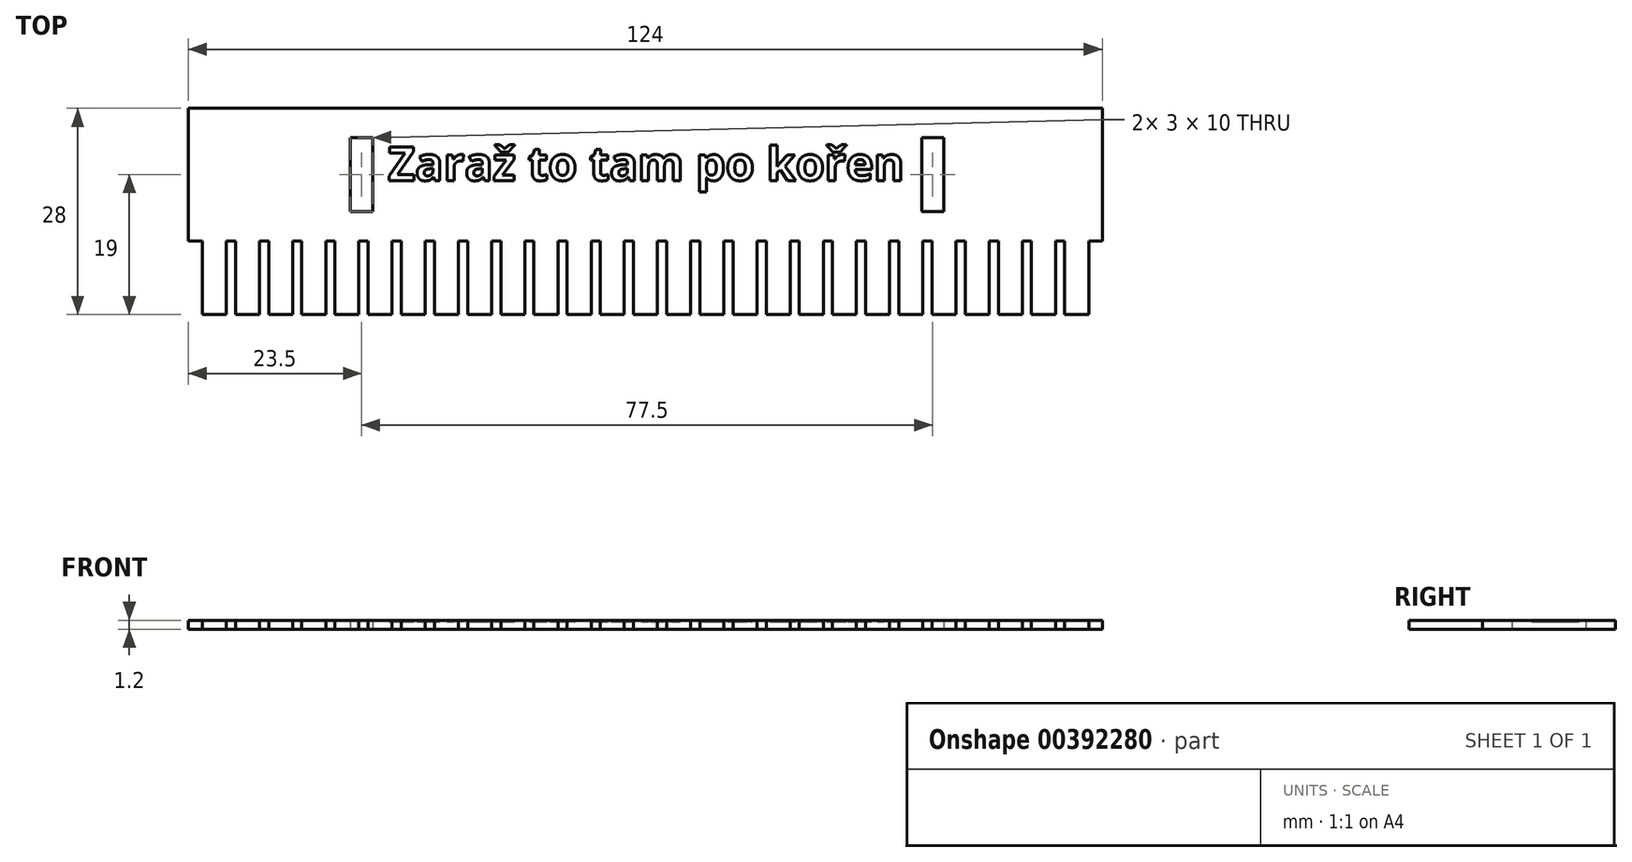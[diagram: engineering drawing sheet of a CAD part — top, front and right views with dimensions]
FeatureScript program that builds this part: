
annotation { "Feature Type Name" : "Feature", "Feature Type Description" : "" }
export const myFeature = defineFeature(function(context is Context, id is Id, definition is map)
    precondition{}
    {
        {
            var Q0;
            Q0=qCreatedBy(makeId("Top.planeOp"),FACE);
            var sketch = newSketch(context, id + "F0", { "sketchPlane" : qUnion([Q0])});
            skLineSegment(sketch, "E0.bottom", {"start": v(62, -14) * mm, "end": v(-62, -14) * mm});
            skLineSegment(sketch, "E0.top", {"start": v(62, 14) * mm, "end": v(-62, 14) * mm});
            skLineSegment(sketch, "E0.left", {"start": v(62, -14) * mm, "end": v(62, 14) * mm});
            skLineSegment(sketch, "E0.right", {"start": v(-62, -14) * mm, "end": v(-62, 14) * mm});
            skPoint(sketch, "E0.middle", {"position": v(0, 0) * mm});
            skLineSegment(sketch, "E1.bottom", {"start": v(-62, -14) * mm, "end": v(-60.1, -14) * mm});
            skLineSegment(sketch, "E1.top", {"start": v(-62, -4) * mm, "end": v(-60.1, -4) * mm});
            skLineSegment(sketch, "E1.left", {"start": v(-62, -14) * mm, "end": v(-62, -4) * mm});
            skLineSegment(sketch, "E1.right", {"start": v(-60.1, -14) * mm, "end": v(-60.1, -4) * mm});
            skLineSegment(sketch, "E2.bottom", {"start": v(-60.1, -14) * mm, "end": v(-56.85, -14) * mm});
            skLineSegment(sketch, "E2.right", {"start": v(-56.85, -14) * mm, "end": v(-56.85, -4) * mm});
            skLineSegment(sketch, "E3.bottom", {"start": v(-56.85, -14) * mm, "end": v(-55.6, -14) * mm});
            skLineSegment(sketch, "E3.top", {"start": v(-56.85, -4) * mm, "end": v(-55.6, -4) * mm});
            skLineSegment(sketch, "E3.right", {"start": v(-55.6, -14) * mm, "end": v(-55.6, -4) * mm});
            skLineSegment(sketch, "E4.bottom", {"start": v(-55.6, -14) * mm, "end": v(-52.35, -14) * mm});
            skLineSegment(sketch, "E4.right", {"start": v(-52.35, -14) * mm, "end": v(-52.35, -4) * mm});
            skLineSegment(sketch, "E5.bottom", {"start": v(-52.35, -14) * mm, "end": v(-51.1, -14) * mm});
            skLineSegment(sketch, "E5.top", {"start": v(-52.35, -4) * mm, "end": v(-51.1, -4) * mm});
            skLineSegment(sketch, "E5.right", {"start": v(-51.1, -14) * mm, "end": v(-51.1, -4) * mm});
            skLineSegment(sketch, "E6.bottom", {"start": v(-51.1, -14) * mm, "end": v(-47.85, -14) * mm});
            skLineSegment(sketch, "E6.right", {"start": v(-47.85, -14) * mm, "end": v(-47.85, -4) * mm});
            skLineSegment(sketch, "E7.bottom", {"start": v(-47.85, -14) * mm, "end": v(-46.6, -14) * mm});
            skLineSegment(sketch, "E7.top", {"start": v(-47.85, -4) * mm, "end": v(-46.6, -4) * mm});
            skLineSegment(sketch, "E7.right", {"start": v(-46.6, -14) * mm, "end": v(-46.6, -4) * mm});
            skLineSegment(sketch, "E8.bottom", {"start": v(-46.6, -14) * mm, "end": v(-43.35, -14) * mm});
            skLineSegment(sketch, "E8.right", {"start": v(-43.35, -14) * mm, "end": v(-43.35, -4) * mm});
            skLineSegment(sketch, "E9.bottom", {"start": v(-43.35, -14) * mm, "end": v(-42.1, -14) * mm});
            skLineSegment(sketch, "E9.top", {"start": v(-43.35, -4) * mm, "end": v(-42.1, -4) * mm});
            skLineSegment(sketch, "E9.right", {"start": v(-42.1, -14) * mm, "end": v(-42.1, -4) * mm});
            skLineSegment(sketch, "E10.bottom", {"start": v(-42.1, -14) * mm, "end": v(-38.85, -14) * mm});
            skLineSegment(sketch, "E10.right", {"start": v(-38.85, -14) * mm, "end": v(-38.85, -4) * mm});
            skLineSegment(sketch, "E11.bottom", {"start": v(-38.85, -14) * mm, "end": v(-37.6, -14) * mm});
            skLineSegment(sketch, "E11.top", {"start": v(-38.85, -4) * mm, "end": v(-37.6, -4) * mm});
            skLineSegment(sketch, "E11.right", {"start": v(-37.6, -14) * mm, "end": v(-37.6, -4) * mm});
            skLineSegment(sketch, "E12.bottom", {"start": v(-37.6, -14) * mm, "end": v(-34.35, -14) * mm});
            skLineSegment(sketch, "E12.right", {"start": v(-34.35, -14) * mm, "end": v(-34.35, -4) * mm});
            skLineSegment(sketch, "E13.bottom", {"start": v(-34.35, -14) * mm, "end": v(-33.1, -14) * mm});
            skLineSegment(sketch, "E13.top", {"start": v(-34.35, -4) * mm, "end": v(-33.1, -4) * mm});
            skLineSegment(sketch, "E13.right", {"start": v(-33.1, -14) * mm, "end": v(-33.1, -4) * mm});
            skLineSegment(sketch, "E14.bottom", {"start": v(-33.1, -14) * mm, "end": v(-29.85, -14) * mm});
            skLineSegment(sketch, "E14.right", {"start": v(-29.85, -14) * mm, "end": v(-29.85, -4) * mm});
            skLineSegment(sketch, "E15.bottom", {"start": v(-29.85, -14) * mm, "end": v(-28.6, -14) * mm});
            skLineSegment(sketch, "E15.top", {"start": v(-29.85, -4) * mm, "end": v(-28.6, -4) * mm});
            skLineSegment(sketch, "E15.right", {"start": v(-28.6, -14) * mm, "end": v(-28.6, -4) * mm});
            skLineSegment(sketch, "E16.bottom", {"start": v(-28.6, -14) * mm, "end": v(-25.35, -14) * mm});
            skLineSegment(sketch, "E16.right", {"start": v(-25.35, -14) * mm, "end": v(-25.35, -4) * mm});
            skLineSegment(sketch, "E17.bottom", {"start": v(-25.35, -14) * mm, "end": v(-24.1, -14) * mm});
            skLineSegment(sketch, "E17.top", {"start": v(-25.35, -4) * mm, "end": v(-24.1, -4) * mm});
            skLineSegment(sketch, "E17.right", {"start": v(-24.1, -14) * mm, "end": v(-24.1, -4) * mm});
            skLineSegment(sketch, "E18.bottom", {"start": v(-24.1, -14) * mm, "end": v(-20.85, -14) * mm});
            skLineSegment(sketch, "E18.right", {"start": v(-20.85, -14) * mm, "end": v(-20.85, -4) * mm});
            skLineSegment(sketch, "E19.bottom", {"start": v(-20.85, -14) * mm, "end": v(-19.6, -14) * mm});
            skLineSegment(sketch, "E19.top", {"start": v(-20.85, -4) * mm, "end": v(-19.6, -4) * mm});
            skLineSegment(sketch, "E19.right", {"start": v(-19.6, -14) * mm, "end": v(-19.6, -4) * mm});
            skLineSegment(sketch, "E20.bottom", {"start": v(-19.6, -14) * mm, "end": v(-16.35, -14) * mm});
            skLineSegment(sketch, "E20.right", {"start": v(-16.35, -14) * mm, "end": v(-16.35, -4) * mm});
            skLineSegment(sketch, "E21.bottom", {"start": v(-16.35, -14) * mm, "end": v(-15.1, -14) * mm});
            skLineSegment(sketch, "E21.top", {"start": v(-16.35, -4) * mm, "end": v(-15.1, -4) * mm});
            skLineSegment(sketch, "E21.right", {"start": v(-15.1, -14) * mm, "end": v(-15.1, -4) * mm});
            skLineSegment(sketch, "E22.bottom", {"start": v(-15.1, -14) * mm, "end": v(-11.85, -14) * mm});
            skLineSegment(sketch, "E22.right", {"start": v(-11.85, -14) * mm, "end": v(-11.85, -4) * mm});
            skLineSegment(sketch, "E23.bottom", {"start": v(-11.85, -14) * mm, "end": v(-10.6, -14) * mm});
            skLineSegment(sketch, "E23.top", {"start": v(-11.85, -4) * mm, "end": v(-10.6, -4) * mm});
            skLineSegment(sketch, "E23.right", {"start": v(-10.6, -14) * mm, "end": v(-10.6, -4) * mm});
            skLineSegment(sketch, "E24.bottom", {"start": v(-10.6, -14) * mm, "end": v(-7.35, -14) * mm});
            skLineSegment(sketch, "E24.right", {"start": v(-7.35, -14) * mm, "end": v(-7.35, -4) * mm});
            skLineSegment(sketch, "E25.bottom", {"start": v(-7.35, -14) * mm, "end": v(-6.1, -14) * mm});
            skLineSegment(sketch, "E25.top", {"start": v(-7.35, -4) * mm, "end": v(-6.1, -4) * mm});
            skLineSegment(sketch, "E25.right", {"start": v(-6.1, -14) * mm, "end": v(-6.1, -4) * mm});
            skLineSegment(sketch, "E26.bottom", {"start": v(-6.1, -14) * mm, "end": v(-2.85, -14) * mm});
            skLineSegment(sketch, "E26.right", {"start": v(-2.85, -14) * mm, "end": v(-2.85, -4) * mm});
            skLineSegment(sketch, "E27.bottom", {"start": v(-2.85, -14) * mm, "end": v(-1.6, -14) * mm});
            skLineSegment(sketch, "E27.top", {"start": v(-2.85, -4) * mm, "end": v(-1.6, -4) * mm});
            skLineSegment(sketch, "E27.right", {"start": v(-1.6, -14) * mm, "end": v(-1.6, -4) * mm});
            skLineSegment(sketch, "E28.bottom", {"start": v(-1.6, -14) * mm, "end": v(1.65, -14) * mm});
            skLineSegment(sketch, "E28.right", {"start": v(1.65, -14) * mm, "end": v(1.65, -4) * mm});
            skLineSegment(sketch, "E29.bottom", {"start": v(1.65, -14) * mm, "end": v(2.9, -14) * mm});
            skLineSegment(sketch, "E29.top", {"start": v(1.65, -4) * mm, "end": v(2.9, -4) * mm});
            skLineSegment(sketch, "E29.right", {"start": v(2.9, -14) * mm, "end": v(2.9, -4) * mm});
            skLineSegment(sketch, "E30.bottom", {"start": v(2.9, -14) * mm, "end": v(6.15, -14) * mm});
            skLineSegment(sketch, "E30.right", {"start": v(6.15, -14) * mm, "end": v(6.15, -4) * mm});
            skLineSegment(sketch, "E31.bottom", {"start": v(6.15, -14) * mm, "end": v(7.4, -14) * mm});
            skLineSegment(sketch, "E31.top", {"start": v(6.15, -4) * mm, "end": v(7.4, -4) * mm});
            skLineSegment(sketch, "E31.right", {"start": v(7.4, -14) * mm, "end": v(7.4, -4) * mm});
            skLineSegment(sketch, "E32.bottom", {"start": v(7.4, -14) * mm, "end": v(10.65, -14) * mm});
            skLineSegment(sketch, "E32.right", {"start": v(10.65, -14) * mm, "end": v(10.65, -4) * mm});
            skLineSegment(sketch, "E33.bottom", {"start": v(10.65, -14) * mm, "end": v(11.9, -14) * mm});
            skLineSegment(sketch, "E33.top", {"start": v(10.65, -4) * mm, "end": v(11.9, -4) * mm});
            skLineSegment(sketch, "E33.right", {"start": v(11.9, -14) * mm, "end": v(11.9, -4) * mm});
            skLineSegment(sketch, "E34.bottom", {"start": v(11.9, -14) * mm, "end": v(15.15, -14) * mm});
            skLineSegment(sketch, "E34.right", {"start": v(15.15, -14) * mm, "end": v(15.15, -4) * mm});
            skLineSegment(sketch, "E35.bottom", {"start": v(15.15, -14) * mm, "end": v(16.4, -14) * mm});
            skLineSegment(sketch, "E35.top", {"start": v(15.15, -4) * mm, "end": v(16.4, -4) * mm});
            skLineSegment(sketch, "E35.right", {"start": v(16.4, -14) * mm, "end": v(16.4, -4) * mm});
            skLineSegment(sketch, "E36.bottom", {"start": v(16.4, -14) * mm, "end": v(19.65, -14) * mm});
            skLineSegment(sketch, "E36.right", {"start": v(19.65, -14) * mm, "end": v(19.65, -4) * mm});
            skLineSegment(sketch, "E37.bottom", {"start": v(19.65, -14) * mm, "end": v(20.9, -14) * mm});
            skLineSegment(sketch, "E37.top", {"start": v(19.65, -4) * mm, "end": v(20.9, -4) * mm});
            skLineSegment(sketch, "E37.right", {"start": v(20.9, -14) * mm, "end": v(20.9, -4) * mm});
            skLineSegment(sketch, "E38.bottom", {"start": v(20.9, -14) * mm, "end": v(24.15, -14) * mm});
            skLineSegment(sketch, "E38.right", {"start": v(24.15, -14) * mm, "end": v(24.15, -4) * mm});
            skLineSegment(sketch, "E39.bottom", {"start": v(24.15, -14) * mm, "end": v(25.4, -14) * mm});
            skLineSegment(sketch, "E39.top", {"start": v(24.15, -4) * mm, "end": v(25.4, -4) * mm});
            skLineSegment(sketch, "E39.right", {"start": v(25.4, -14) * mm, "end": v(25.4, -4) * mm});
            skLineSegment(sketch, "E40.bottom", {"start": v(25.4, -14) * mm, "end": v(28.65, -14) * mm});
            skLineSegment(sketch, "E40.right", {"start": v(28.65, -14) * mm, "end": v(28.65, -4) * mm});
            skLineSegment(sketch, "E41.bottom", {"start": v(28.65, -14) * mm, "end": v(29.9, -14) * mm});
            skLineSegment(sketch, "E41.top", {"start": v(28.65, -4) * mm, "end": v(29.9, -4) * mm});
            skLineSegment(sketch, "E41.right", {"start": v(29.9, -14) * mm, "end": v(29.9, -4) * mm});
            skLineSegment(sketch, "E42.bottom", {"start": v(29.9, -14) * mm, "end": v(33.15, -14) * mm});
            skLineSegment(sketch, "E42.right", {"start": v(33.15, -14) * mm, "end": v(33.15, -4) * mm});
            skLineSegment(sketch, "E43.bottom", {"start": v(33.15, -14) * mm, "end": v(34.4, -14) * mm});
            skLineSegment(sketch, "E43.top", {"start": v(33.15, -4) * mm, "end": v(34.4, -4) * mm});
            skLineSegment(sketch, "E43.right", {"start": v(34.4, -14) * mm, "end": v(34.4, -4) * mm});
            skLineSegment(sketch, "E44.bottom", {"start": v(34.4, -14) * mm, "end": v(37.65, -14) * mm});
            skLineSegment(sketch, "E44.right", {"start": v(37.65, -14) * mm, "end": v(37.65, -4) * mm});
            skLineSegment(sketch, "E45.bottom", {"start": v(37.65, -14) * mm, "end": v(38.9, -14) * mm});
            skLineSegment(sketch, "E45.top", {"start": v(37.65, -4) * mm, "end": v(38.9, -4) * mm});
            skLineSegment(sketch, "E45.right", {"start": v(38.9, -14) * mm, "end": v(38.9, -4) * mm});
            skLineSegment(sketch, "E46.bottom", {"start": v(38.9, -14) * mm, "end": v(42.15, -14) * mm});
            skLineSegment(sketch, "E46.right", {"start": v(42.15, -14) * mm, "end": v(42.15, -4) * mm});
            skLineSegment(sketch, "E47.bottom", {"start": v(42.15, -14) * mm, "end": v(43.4, -14) * mm});
            skLineSegment(sketch, "E47.top", {"start": v(42.15, -4) * mm, "end": v(43.4, -4) * mm});
            skLineSegment(sketch, "E47.right", {"start": v(43.4, -14) * mm, "end": v(43.4, -4) * mm});
            skLineSegment(sketch, "E48.bottom", {"start": v(43.4, -14) * mm, "end": v(46.65, -14) * mm});
            skLineSegment(sketch, "E48.right", {"start": v(46.65, -14) * mm, "end": v(46.65, -4) * mm});
            skLineSegment(sketch, "E49.bottom", {"start": v(46.65, -14) * mm, "end": v(47.9, -14) * mm});
            skLineSegment(sketch, "E49.top", {"start": v(46.65, -4) * mm, "end": v(47.9, -4) * mm});
            skLineSegment(sketch, "E49.right", {"start": v(47.9, -14) * mm, "end": v(47.9, -4) * mm});
            skLineSegment(sketch, "E50.bottom", {"start": v(47.9, -14) * mm, "end": v(51.15, -14) * mm});
            skLineSegment(sketch, "E50.right", {"start": v(51.15, -14) * mm, "end": v(51.15, -4) * mm});
            skLineSegment(sketch, "E51.bottom", {"start": v(51.15, -14) * mm, "end": v(52.4, -14) * mm});
            skLineSegment(sketch, "E51.top", {"start": v(51.15, -4) * mm, "end": v(52.4, -4) * mm});
            skLineSegment(sketch, "E51.right", {"start": v(52.4, -14) * mm, "end": v(52.4, -4) * mm});
            skLineSegment(sketch, "E52.bottom", {"start": v(52.4, -14) * mm, "end": v(55.65, -14) * mm});
            skLineSegment(sketch, "E52.right", {"start": v(55.65, -14) * mm, "end": v(55.65, -4) * mm});
            skLineSegment(sketch, "E53.bottom", {"start": v(55.65, -14) * mm, "end": v(56.9, -14) * mm});
            skLineSegment(sketch, "E53.top", {"start": v(55.65, -4) * mm, "end": v(56.9, -4) * mm});
            skLineSegment(sketch, "E53.right", {"start": v(56.9, -14) * mm, "end": v(56.9, -4) * mm});
            skLineSegment(sketch, "E54.bottom", {"start": v(56.9, -14) * mm, "end": v(60.15, -14) * mm});
            skLineSegment(sketch, "E54.right", {"start": v(60.15, -14) * mm, "end": v(60.15, -4) * mm});
            skLineSegment(sketch, "E55.bottom", {"start": v(60.15, -14) * mm, "end": v(62.05, -14) * mm});
            skLineSegment(sketch, "E55.top", {"start": v(60.15, -4) * mm, "end": v(62.05, -4) * mm});
            skLineSegment(sketch, "E55.right", {"start": v(62.05, -14) * mm, "end": v(62.05, -4) * mm});
            skLineSegment(sketch, "E56.bottom", {"start": v(-37, 0) * mm, "end": v(-40, 0) * mm});
            skLineSegment(sketch, "E56.top", {"start": v(-37, 10) * mm, "end": v(-40, 10) * mm});
            skLineSegment(sketch, "E56.left", {"start": v(-37, 0) * mm, "end": v(-37, 10) * mm});
            skLineSegment(sketch, "E56.right", {"start": v(-40, 0) * mm, "end": v(-40, 10) * mm});
            skPoint(sketch, "E56.middle", {"position": v(-38.5, 5) * mm});
            skLineSegment(sketch, "E57.bottom", {"start": v(-40, 10) * mm, "end": v(-37, 10) * mm});
            skLineSegment(sketch, "E57.top", {"start": v(-40, 14) * mm, "end": v(-37, 14) * mm});
            skLineSegment(sketch, "E58.left", {"start": v(-40, 10) * mm, "end": v(-40, 0) * mm});
            skLineSegment(sketch, "E58.right", {"start": v(-62, 10) * mm, "end": v(-62, 0) * mm});
            skLineSegment(sketch, "E59.left", {"start": v(-37, 10) * mm, "end": v(-37, 0) * mm});
            skLineSegment(sketch, "E59.right", {"start": v(37.5, 10) * mm, "end": v(37.5, 0) * mm});
            skLineSegment(sketch, "E60.bottom", {"start": v(37.5, 10) * mm, "end": v(40.5, 10) * mm});
            skLineSegment(sketch, "E60.top", {"start": v(37.5, 0) * mm, "end": v(40.5, 0) * mm});
            skLineSegment(sketch, "E60.right", {"start": v(40.5, 10) * mm, "end": v(40.5, 0) * mm});
            skLineSegment(sketch, "E61.right", {"start": v(62, 10) * mm, "end": v(62, 0) * mm});
            skSolve(sketch);
        }
        {
            var Q0;
            {var subQ9=sQuery(id+"F0.wireOp",EDGE,"E1.top");Q0=makeQuery(id+"F0.imprint","IMPRINT",FACE,{"disambiguationData":[TD([[makeQuery(id+"F0.imprint","IMPRINT",EDGE,{"derivedFrom":subQ9}),1.0]])]});}
            extrude(context, id + "F1", {"entities" : qUnion([Q0]), "depth" : 1.2 * mm});
        }
        {
            var Q0;
            Q0=makeQuery(id+"F1.opExtrude","CAP_FACE",FACE,{"disambiguationData":[OSD([sQuery(id+"F0.wireOp",EDGE,"E0.top"),sQuery(id+"F0.wireOp",EDGE,"E0.left"),sQuery(id+"F0.wireOp",EDGE,"E0.right"),sQuery(id+"F0.wireOp",EDGE,"E1.top"),sQuery(id+"F0.wireOp",EDGE,"E2.bottom"),sQuery(id+"F0.wireOp",EDGE,"E1.right"),sQuery(id+"F0.wireOp",EDGE,"E3.top"),sQuery(id+"F0.wireOp",EDGE,"E2.right"),sQuery(id+"F0.wireOp",EDGE,"E4.bottom"),sQuery(id+"F0.wireOp",EDGE,"E3.right"),sQuery(id+"F0.wireOp",EDGE,"E5.top"),sQuery(id+"F0.wireOp",EDGE,"E4.right"),sQuery(id+"F0.wireOp",EDGE,"E6.bottom"),sQuery(id+"F0.wireOp",EDGE,"E5.right"),sQuery(id+"F0.wireOp",EDGE,"E7.top"),sQuery(id+"F0.wireOp",EDGE,"E6.right"),sQuery(id+"F0.wireOp",EDGE,"E8.bottom"),sQuery(id+"F0.wireOp",EDGE,"E7.right"),sQuery(id+"F0.wireOp",EDGE,"E9.top"),sQuery(id+"F0.wireOp",EDGE,"E8.right"),sQuery(id+"F0.wireOp",EDGE,"E10.bottom"),sQuery(id+"F0.wireOp",EDGE,"E9.right"),sQuery(id+"F0.wireOp",EDGE,"E11.top"),sQuery(id+"F0.wireOp",EDGE,"E10.right"),sQuery(id+"F0.wireOp",EDGE,"E12.bottom"),sQuery(id+"F0.wireOp",EDGE,"E11.right"),sQuery(id+"F0.wireOp",EDGE,"E13.top"),sQuery(id+"F0.wireOp",EDGE,"E12.right"),sQuery(id+"F0.wireOp",EDGE,"E14.bottom"),sQuery(id+"F0.wireOp",EDGE,"E13.right"),sQuery(id+"F0.wireOp",EDGE,"E15.top"),sQuery(id+"F0.wireOp",EDGE,"E14.right"),sQuery(id+"F0.wireOp",EDGE,"E16.bottom"),sQuery(id+"F0.wireOp",EDGE,"E15.right"),sQuery(id+"F0.wireOp",EDGE,"E17.top"),sQuery(id+"F0.wireOp",EDGE,"E16.right"),sQuery(id+"F0.wireOp",EDGE,"E18.bottom"),sQuery(id+"F0.wireOp",EDGE,"E17.right"),sQuery(id+"F0.wireOp",EDGE,"E19.top"),sQuery(id+"F0.wireOp",EDGE,"E18.right"),sQuery(id+"F0.wireOp",EDGE,"E20.bottom"),sQuery(id+"F0.wireOp",EDGE,"E19.right"),sQuery(id+"F0.wireOp",EDGE,"E21.top"),sQuery(id+"F0.wireOp",EDGE,"E20.right"),sQuery(id+"F0.wireOp",EDGE,"E22.bottom"),sQuery(id+"F0.wireOp",EDGE,"E21.right"),sQuery(id+"F0.wireOp",EDGE,"E23.top"),sQuery(id+"F0.wireOp",EDGE,"E22.right"),sQuery(id+"F0.wireOp",EDGE,"E24.bottom"),sQuery(id+"F0.wireOp",EDGE,"E23.right"),sQuery(id+"F0.wireOp",EDGE,"E25.top"),sQuery(id+"F0.wireOp",EDGE,"E24.right"),sQuery(id+"F0.wireOp",EDGE,"E26.bottom"),sQuery(id+"F0.wireOp",EDGE,"E25.right"),sQuery(id+"F0.wireOp",EDGE,"E27.top"),sQuery(id+"F0.wireOp",EDGE,"E26.right"),sQuery(id+"F0.wireOp",EDGE,"E28.bottom"),sQuery(id+"F0.wireOp",EDGE,"E27.right"),sQuery(id+"F0.wireOp",EDGE,"E29.top"),sQuery(id+"F0.wireOp",EDGE,"E28.right"),sQuery(id+"F0.wireOp",EDGE,"E30.bottom"),sQuery(id+"F0.wireOp",EDGE,"E29.right"),sQuery(id+"F0.wireOp",EDGE,"E31.top"),sQuery(id+"F0.wireOp",EDGE,"E30.right"),sQuery(id+"F0.wireOp",EDGE,"E32.bottom"),sQuery(id+"F0.wireOp",EDGE,"E31.right"),sQuery(id+"F0.wireOp",EDGE,"E33.top"),sQuery(id+"F0.wireOp",EDGE,"E32.right"),sQuery(id+"F0.wireOp",EDGE,"E34.bottom"),sQuery(id+"F0.wireOp",EDGE,"E33.right"),sQuery(id+"F0.wireOp",EDGE,"E35.top"),sQuery(id+"F0.wireOp",EDGE,"E34.right"),sQuery(id+"F0.wireOp",EDGE,"E36.bottom"),sQuery(id+"F0.wireOp",EDGE,"E35.right"),sQuery(id+"F0.wireOp",EDGE,"E37.top"),sQuery(id+"F0.wireOp",EDGE,"E36.right"),sQuery(id+"F0.wireOp",EDGE,"E38.bottom"),sQuery(id+"F0.wireOp",EDGE,"E37.right"),sQuery(id+"F0.wireOp",EDGE,"E39.top"),sQuery(id+"F0.wireOp",EDGE,"E38.right"),sQuery(id+"F0.wireOp",EDGE,"E40.bottom"),sQuery(id+"F0.wireOp",EDGE,"E39.right"),sQuery(id+"F0.wireOp",EDGE,"E41.top"),sQuery(id+"F0.wireOp",EDGE,"E40.right"),sQuery(id+"F0.wireOp",EDGE,"E42.bottom"),sQuery(id+"F0.wireOp",EDGE,"E41.right"),sQuery(id+"F0.wireOp",EDGE,"E43.top"),sQuery(id+"F0.wireOp",EDGE,"E42.right"),sQuery(id+"F0.wireOp",EDGE,"E44.bottom"),sQuery(id+"F0.wireOp",EDGE,"E43.right"),sQuery(id+"F0.wireOp",EDGE,"E45.top"),sQuery(id+"F0.wireOp",EDGE,"E44.right"),sQuery(id+"F0.wireOp",EDGE,"E46.bottom"),sQuery(id+"F0.wireOp",EDGE,"E45.right"),sQuery(id+"F0.wireOp",EDGE,"E47.top"),sQuery(id+"F0.wireOp",EDGE,"E46.right"),sQuery(id+"F0.wireOp",EDGE,"E48.bottom"),sQuery(id+"F0.wireOp",EDGE,"E47.right"),sQuery(id+"F0.wireOp",EDGE,"E49.top"),sQuery(id+"F0.wireOp",EDGE,"E48.right"),sQuery(id+"F0.wireOp",EDGE,"E50.bottom"),sQuery(id+"F0.wireOp",EDGE,"E49.right"),sQuery(id+"F0.wireOp",EDGE,"E51.top"),sQuery(id+"F0.wireOp",EDGE,"E50.right"),sQuery(id+"F0.wireOp",EDGE,"E52.bottom"),sQuery(id+"F0.wireOp",EDGE,"E51.right"),sQuery(id+"F0.wireOp",EDGE,"E53.top"),sQuery(id+"F0.wireOp",EDGE,"E52.right"),sQuery(id+"F0.wireOp",EDGE,"E54.bottom"),sQuery(id+"F0.wireOp",EDGE,"E53.right"),sQuery(id+"F0.wireOp",EDGE,"E55.top"),sQuery(id+"F0.wireOp",EDGE,"E54.right"),sQuery(id+"F0.wireOp",EDGE,"E56.bottom"),sQuery(id+"F0.wireOp",EDGE,"E57.bottom"),sQuery(id+"F0.wireOp",EDGE,"E57.top"),sQuery(id+"F0.wireOp",EDGE,"E58.left"),sQuery(id+"F0.wireOp",EDGE,"E58.right"),sQuery(id+"F0.wireOp",EDGE,"E59.left"),sQuery(id+"F0.wireOp",EDGE,"E60.bottom"),sQuery(id+"F0.wireOp",EDGE,"E60.top"),sQuery(id+"F0.wireOp",EDGE,"E59.right"),sQuery(id+"F0.wireOp",EDGE,"E60.right"),sQuery(id+"F0.wireOp",EDGE,"E61.right")])],"isStart":false});
            var sketch = newSketch(context, id + "F2", { "sketchPlane" : qUnion([Q0])});
            skText(sketch, "E62", { "text": "Zaraž to tam po kořen", "fontName": "OpenSans-Bold.ttf"});
            const initialGuessF2  = {"E62": [-0.0349, 0.0042, 1, 0, 0.00457]};
            skSetInitialGuess(sketch, initialGuessF2);
            skSolve(sketch);
        }
        {
            var Q0;
            Q0=qSketchRegion(id+"F2",true);
            var Q1;
            Q1=qConstructionFilter(qBodyType(qCreatedBy(id+"F2",EDGE),BodyType.WIRE),ConstructionObject.NO);
            extrude(context, id + "F3", {"entities" : qUnion([Q0]), "operationType" : NewBodyOperationType.REMOVE, "surfaceEntities" : qUnion([Q1]), "depth" : -0.2 * mm});
        }
    });
